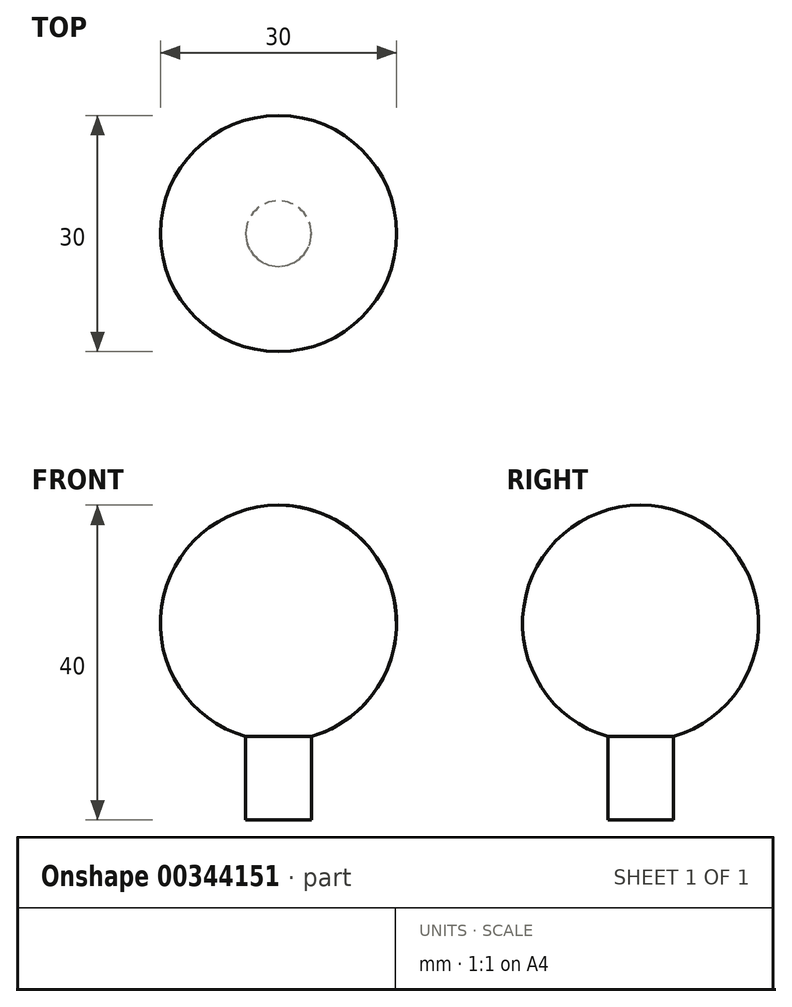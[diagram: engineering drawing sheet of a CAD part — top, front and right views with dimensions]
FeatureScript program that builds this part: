
annotation { "Feature Type Name" : "Feature", "Feature Type Description" : "" }
export const myFeature = defineFeature(function(context is Context, id is Id, definition is map)
    precondition{}
    {
        {
            var Q0;
            Q0=qCreatedBy(makeId("Front.planeOp"),FACE);
            var sketch = newSketch(context, id + "F0", { "sketchPlane" : qUnion([Q0])});
            skLineSegment(sketch, "E0", {"start": v(0, 0) * mm, "end": v(0, -30) * mm});
            skArc(sketch, "E1", {"start": v(0, -30) * mm, "mid": v(15, -15) * mm, "end": v(0, 0) * mm});
            skLineSegment(sketch, "E2", {"start": v(4.17, -29.4) * mm, "end": v(4.17, -40) * mm});
            skLineSegment(sketch, "E3", {"start": v(4.17, -40) * mm, "end": v(0, -40) * mm});
            skLineSegment(sketch, "E4", {"start": v(0, -40) * mm, "end": v(0, -30) * mm});
            skSolve(sketch);
        }
        {
            var Q0;
            {var subQ0=sQuery(id+"F0.wireOp",EDGE,"E0");Q0=makeQuery(id+"F0.imprint","IMPRINT",FACE,{"disambiguationData":[TD([[makeQuery(id+"F0.imprint","IMPRINT",EDGE,{"derivedFrom":subQ0}),1.0]])]});}
            var Q1;
            {var subQ2=sQuery(id+"F0.wireOp",EDGE,"E2");Q1=makeQuery(id+"F0.imprint","IMPRINT",FACE,{"disambiguationData":[TD([[makeQuery(id+"F0.imprint","IMPRINT",EDGE,{"derivedFrom":subQ2}),-1.0]])]});}
            var Q2;
            Q2=sQuery(id+"F0.wireOp",EDGE,"E4");
            revolve(context, id + "F1", {"entities" : qUnion([Q0, Q1]), "axis" : qUnion([Q2]), "revolveType" : RevolveType.FULL});
        }
    });
